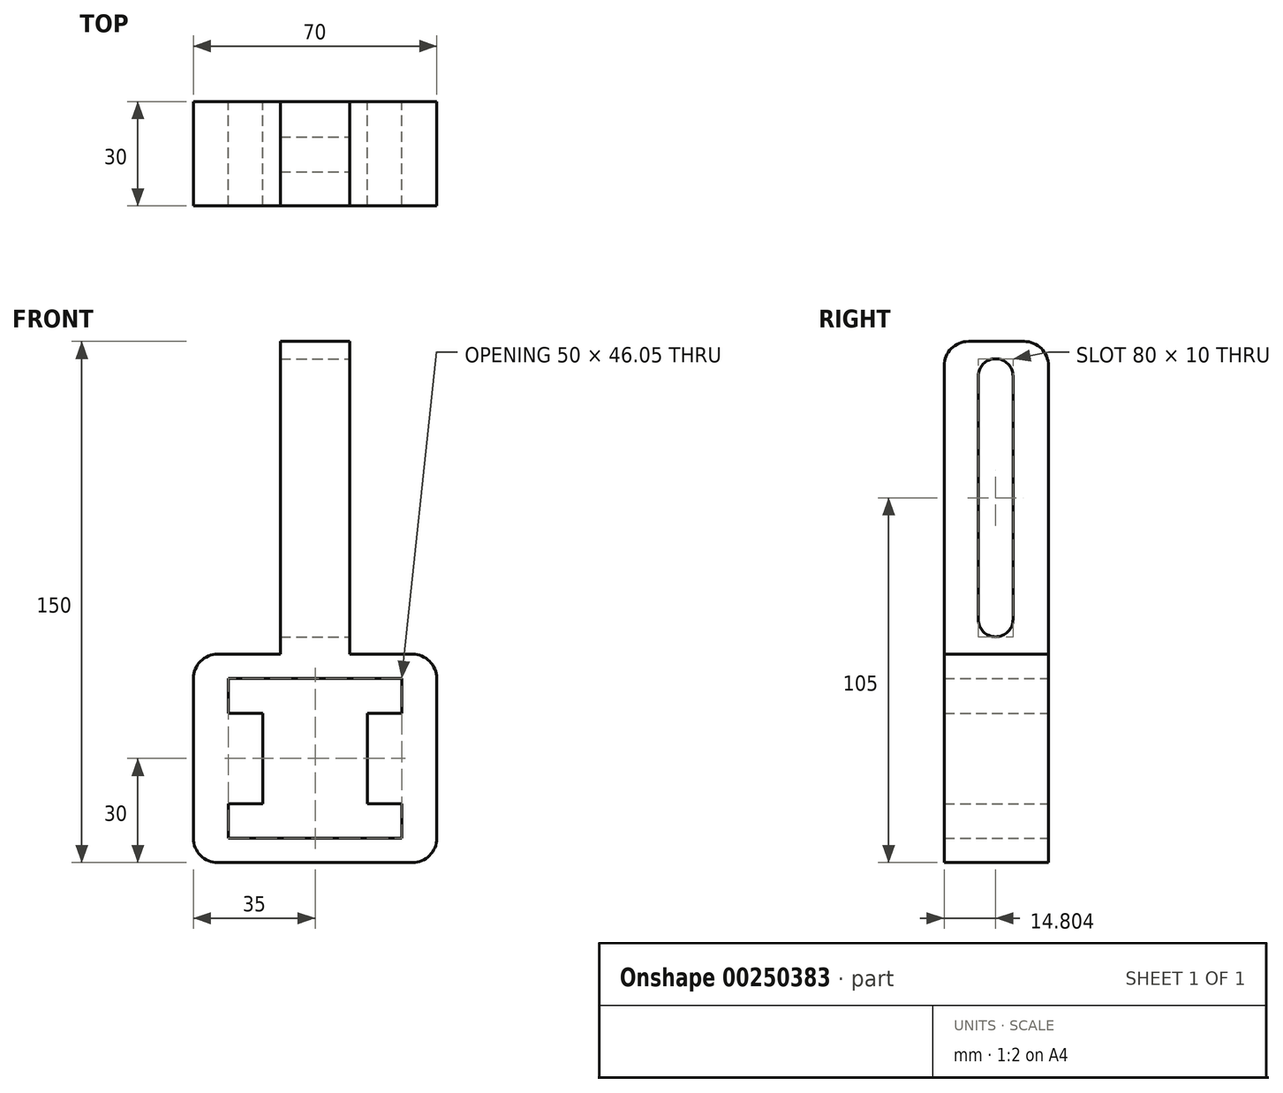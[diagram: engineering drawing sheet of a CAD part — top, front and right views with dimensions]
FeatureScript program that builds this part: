
annotation { "Feature Type Name" : "Feature", "Feature Type Description" : "" }
export const myFeature = defineFeature(function(context is Context, id is Id, definition is map)
    precondition{}
    {
        {
            var Q0;
            Q0=qCreatedBy(makeId("Front.planeOp"),FACE);
            var sketch = newSketch(context, id + "F0", { "sketchPlane" : qUnion([Q0])});
            skLineSegment(sketch, "E0.bottom", {"start": v(28, -30) * mm, "end": v(-28, -30) * mm});
            skLineSegment(sketch, "E0.top", {"start": v(28, 30) * mm, "end": v(-28, 30) * mm});
            skLineSegment(sketch, "E0.left", {"start": v(35, -23) * mm, "end": v(35, 23) * mm});
            skLineSegment(sketch, "E0.right", {"start": v(-35, -23) * mm, "end": v(-35, 23) * mm});
            skPoint(sketch, "E1.visualSharp", {"position": v(-35, 30) * mm});
            skArc(sketch, "E1.filletArc", {"start": v(-28, 30) * mm, "mid": v(-32.95, 27.95) * mm, "end": v(-35, 23) * mm});
            skPoint(sketch, "E2.visualSharp", {"position": v(35, 30) * mm});
            skArc(sketch, "E2.filletArc", {"start": v(35, 23) * mm, "mid": v(32.95, 27.95) * mm, "end": v(28, 30) * mm});
            skPoint(sketch, "E3.visualSharp", {"position": v(35, -30) * mm});
            skArc(sketch, "E3.filletArc", {"start": v(28, -30) * mm, "mid": v(32.95, -27.95) * mm, "end": v(35, -23) * mm});
            skPoint(sketch, "E4.visualSharp", {"position": v(-35, -30) * mm});
            skArc(sketch, "E4.filletArc", {"start": v(-35, -23) * mm, "mid": v(-32.95, -27.95) * mm, "end": v(-28, -30) * mm});
            skArc(sketch, "E5.MirrorCS", {"start": v(35, -23) * mm, "mid": v(32.95, -27.95) * mm, "end": v(28, -30) * mm});
            skLineSegment(sketch, "E6.MirrorCS", {"start": v(35, 23) * mm, "end": v(35, -23) * mm});
            skLineSegment(sketch, "E7", {"start": v(-10, 30) * mm, "end": v(-10, 120) * mm});
            skLineSegment(sketch, "E8", {"start": v(-10, 120) * mm, "end": v(10, 120) * mm});
            skLineSegment(sketch, "E9", {"start": v(10, 120) * mm, "end": v(10, 30) * mm});
            skSolve(sketch);
        }
        {
            var Q0;
            Q0 = qSketchRegion(id + "F0", true);
            extrude(context, id + "F1", {"entities" : qUnion([Q0]), "depth" : 30 * mm});
        }
        {
            var Q0;
            Q0=makeQuery(id+"F1.opExtrude","CAP_FACE",FACE,{"disambiguationData":[OSD([sQuery(id+"F0.wireOp",EDGE,"E0.bottom"),sQuery(id+"F0.wireOp",EDGE,"E0.top"),sQuery(id+"F0.wireOp",EDGE,"E0.right"),sQuery(id+"F0.wireOp",EDGE,"E1.filletArc"),sQuery(id+"F0.wireOp",EDGE,"E2.filletArc"),sQuery(id+"F0.wireOp",EDGE,"E4.filletArc"),sQuery(id+"F0.wireOp",EDGE,"E5.MirrorCS"),sQuery(id+"F0.wireOp",EDGE,"E6.MirrorCS")])],"isStart":false});
            var sketch = newSketch(context, id + "F2", { "sketchPlane" : qUnion([Q0])});
            skPoint(sketch, "E10.middle", {"position": v(0, 0) * mm});
            skLineSegment(sketch, "E11", {"start": v(0, 23.02) * mm, "end": v(-25, 23.02) * mm});
            skLineSegment(sketch, "E12", {"start": v(-25, 23.02) * mm, "end": v(-25, 13.02) * mm});
            skLineSegment(sketch, "E13", {"start": v(-25, 13.02) * mm, "end": v(-15, 13.02) * mm});
            skLineSegment(sketch, "E14", {"start": v(-15, 13.02) * mm, "end": v(-15, -0.3) * mm});
            skLineSegment(sketch, "E15", {"start": v(-54.38, 0) * mm, "end": v(63.7, 0) * mm, "construction": true});
            skLineSegment(sketch, "E16", {"start": v(0, 63.67) * mm, "end": v(0, -46.12) * mm, "construction": true});
            skLineSegment(sketch, "E17.MirrorCS", {"start": v(0, 23.02) * mm, "end": v(25, 23.02) * mm});
            skLineSegment(sketch, "E18.MirrorCS", {"start": v(25, 23.02) * mm, "end": v(25, 13.02) * mm});
            skLineSegment(sketch, "E19.MirrorCS", {"start": v(25, 13.02) * mm, "end": v(15, 13.02) * mm});
            skLineSegment(sketch, "E20.MirrorCS", {"start": v(15, 13.02) * mm, "end": v(15, -0.3) * mm});
            skLineSegment(sketch, "E21.MirrorCS", {"start": v(25, -13.02) * mm, "end": v(15, -13.02) * mm});
            skLineSegment(sketch, "E22.MirrorCS", {"start": v(-25, -13.02) * mm, "end": v(-15, -13.02) * mm});
            skLineSegment(sketch, "E23.MirrorCS", {"start": v(0, -63.67) * mm, "end": v(0, 46.12) * mm, "construction": true});
            skLineSegment(sketch, "E24.MirrorCS", {"start": v(15, -13.02) * mm, "end": v(15, 0.3) * mm});
            skLineSegment(sketch, "E25.MirrorCS", {"start": v(0, -23.02) * mm, "end": v(-25, -23.02) * mm});
            skLineSegment(sketch, "E26.MirrorCS", {"start": v(-25, -23.02) * mm, "end": v(-25, -13.02) * mm});
            skLineSegment(sketch, "E27.MirrorCS", {"start": v(0, -23.02) * mm, "end": v(25, -23.02) * mm});
            skLineSegment(sketch, "E28.MirrorCS", {"start": v(25, -23.02) * mm, "end": v(25, -13.02) * mm});
            skLineSegment(sketch, "E29.MirrorCS", {"start": v(-15, -13.02) * mm, "end": v(-15, 0.3) * mm});
            skSolve(sketch);
        }
        {
            var Q0;
            Q0 = qSketchRegion(id + "F2", true);
            extrude(context, id + "F3", {"entities" : qUnion([Q0]), "endBound" : BoundingType.SYMMETRIC, "depth" : 164 * mm});
        }
        {
            var Q0;
            Q0=makeQuery(id+"F3.opExtrude","SWEPT_BODY",BODY,{"disambiguationData":[OSD([sQuery(id+"F2.wireOp",EDGE,"E11"),sQuery(id+"F2.wireOp",EDGE,"E12"),sQuery(id+"F2.wireOp",EDGE,"E13"),sQuery(id+"F2.wireOp",EDGE,"E14"),sQuery(id+"F2.wireOp",EDGE,"E17.MirrorCS"),sQuery(id+"F2.wireOp",EDGE,"E18.MirrorCS"),sQuery(id+"F2.wireOp",EDGE,"E19.MirrorCS"),sQuery(id+"F2.wireOp",EDGE,"E20.MirrorCS"),sQuery(id+"F2.wireOp",EDGE,"E21.MirrorCS"),sQuery(id+"F2.wireOp",EDGE,"E22.MirrorCS"),sQuery(id+"F2.wireOp",EDGE,"E24.MirrorCS"),sQuery(id+"F2.wireOp",EDGE,"E25.MirrorCS"),sQuery(id+"F2.wireOp",EDGE,"E26.MirrorCS"),sQuery(id+"F2.wireOp",EDGE,"E27.MirrorCS"),sQuery(id+"F2.wireOp",EDGE,"E28.MirrorCS"),sQuery(id+"F2.wireOp",EDGE,"E29.MirrorCS")])]});
            var Q1;
            Q1=makeQuery(id+"F1.opExtrude","SWEPT_BODY",BODY,{"disambiguationData":[OSD([sQuery(id+"F0.wireOp",EDGE,"E0.bottom"),sQuery(id+"F0.wireOp",EDGE,"E0.top"),sQuery(id+"F0.wireOp",EDGE,"E0.right"),sQuery(id+"F0.wireOp",EDGE,"E1.filletArc"),sQuery(id+"F0.wireOp",EDGE,"E2.filletArc"),sQuery(id+"F0.wireOp",EDGE,"E4.filletArc"),sQuery(id+"F0.wireOp",EDGE,"E5.MirrorCS"),sQuery(id+"F0.wireOp",EDGE,"E6.MirrorCS")])]});
            booleanBodies(context, id + "F4", {"operationType" : BooleanOperationType.SUBTRACTION, "tools" : qUnion([Q0]), "targets" : qUnion([Q1])});
        }
        {
            var Q0;
            Q0=makeQuery(id+"F1.opExtrude","CAP_EDGE",EDGE,{"disambiguationData":[OSD([sQuery(id+"F0.wireOp",EDGE,"E8")])],"isStart":false});
            var Q1;
            Q1=makeQuery(id+"F1.opExtrude","CAP_EDGE",EDGE,{"disambiguationData":[OSD([sQuery(id+"F0.wireOp",EDGE,"E8")])],"isStart":true});
            fillet(context, id + "F5", {"entities" : qUnion([Q0, Q1]), "radius" : 7 * mm, "tangentPropagation" : true, "allowEdgeOverflow" : false});
        }
        {
            var Q0;
            Q0=makeQuery(id+"F1.opExtrude","SWEPT_FACE",FACE,{"disambiguationData":[OSD([sQuery(id+"F0.wireOp",EDGE,"E9")])]});
            var sketch = newSketch(context, id + "F6", { "sketchPlane" : qUnion([Q0])});
            skLineSegment(sketch, "E30.bottom", {"start": v(-15.2, 110) * mm, "end": v(-15, 110) * mm});
            skLineSegment(sketch, "E30.top", {"start": v(-15.2, 40) * mm, "end": v(-15, 40) * mm});
            skLineSegment(sketch, "E30.left", {"start": v(-20.2, 110) * mm, "end": v(-20.2, 40) * mm});
            skLineSegment(sketch, "E30.right", {"start": v(-10.2, 110) * mm, "end": v(-10.2, 40) * mm});
            skLineSegment(sketch, "E31", {"start": v(-15, 30) * mm, "end": v(-15, 142.6) * mm, "construction": true});
            skArc(sketch, "E32", {"start": v(-10.2, 110) * mm, "mid": v(-15.2, 115) * mm, "end": v(-20.2, 110) * mm});
            skArc(sketch, "E33", {"start": v(-20.2, 40) * mm, "mid": v(-15.2, 35) * mm, "end": v(-10.2, 40) * mm});
            skSolve(sketch);
        }
        {
            var Q0;
            Q0 = qSketchRegion(id + "F6", true);
            extrude(context, id + "F7", {"entities" : qUnion([Q0]), "oppositeDirection" : true, "depth" : 40.5 * mm});
        }
        {
            var Q0;
            Q0=makeQuery(id+"F7.opExtrude","SWEPT_BODY",BODY,{"disambiguationData":[OSD([sQuery(id+"F6.wireOp",EDGE,"E30.left"),sQuery(id+"F6.wireOp",EDGE,"E30.right"),sQuery(id+"F6.wireOp",EDGE,"E32"),sQuery(id+"F6.wireOp",EDGE,"E33")])]});
            var Q1;
            Q1=makeQuery(id+"F1.opExtrude","SWEPT_BODY",BODY,{"disambiguationData":[OSD([sQuery(id+"F0.wireOp",EDGE,"E0.bottom"),sQuery(id+"F0.wireOp",EDGE,"E0.top"),sQuery(id+"F0.wireOp",EDGE,"E0.right"),sQuery(id+"F0.wireOp",EDGE,"E1.filletArc"),sQuery(id+"F0.wireOp",EDGE,"E2.filletArc"),sQuery(id+"F0.wireOp",EDGE,"E4.filletArc"),sQuery(id+"F0.wireOp",EDGE,"E5.MirrorCS"),sQuery(id+"F0.wireOp",EDGE,"E6.MirrorCS"),sQuery(id+"F0.wireOp",EDGE,"E7"),sQuery(id+"F0.wireOp",EDGE,"E8"),sQuery(id+"F0.wireOp",EDGE,"E9")])]});
            booleanBodies(context, id + "F8", {"operationType" : BooleanOperationType.SUBTRACTION, "tools" : qUnion([Q0]), "targets" : qUnion([Q1])});
        }
    });
